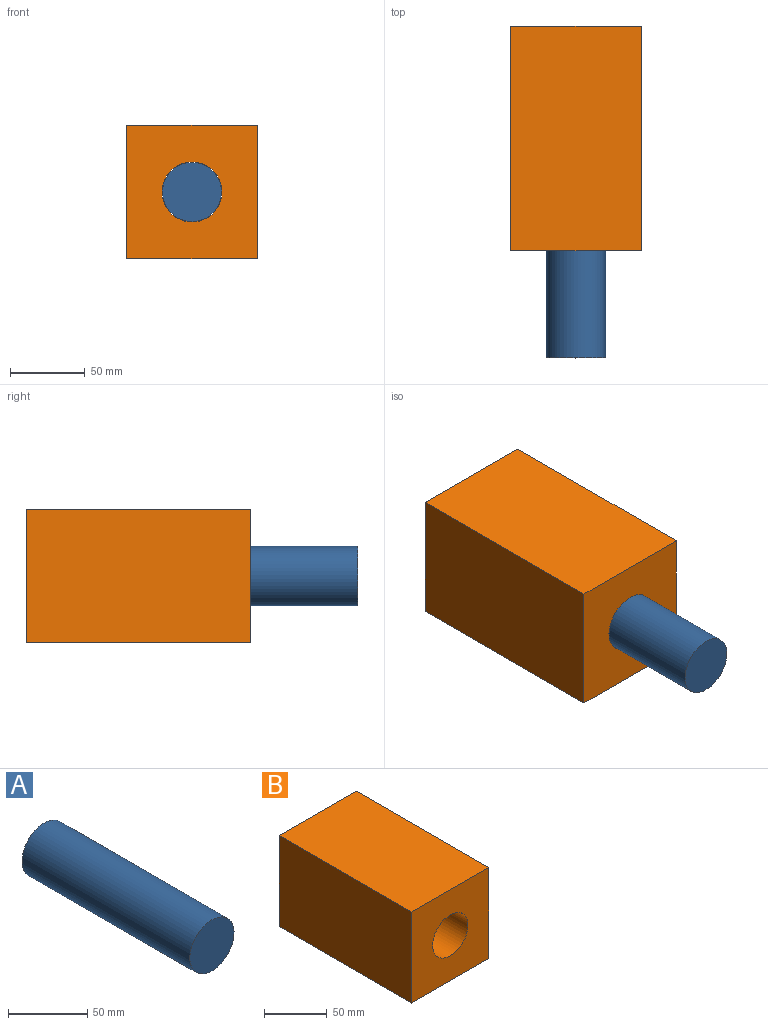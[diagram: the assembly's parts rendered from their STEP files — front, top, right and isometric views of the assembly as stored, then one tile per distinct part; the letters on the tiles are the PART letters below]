
ASSEMBLY  parts=2 mates=1
PART A: 3 faces, bbox 39.5x150x39.5 mm
  f0: cylinder r=19.75mm len=150mm, axis (0,1,0), area 18613.9mm2, adj f1,f2
  f1: plane 39.5x39.5mm, normal (0,-1,0), area 1225.4mm2, adj f0
  f2: plane 39.5x39.5mm, normal (0,1,0), area 1225.4mm2, adj f0
PART B: 7 faces, bbox 87.2x150x89.1 mm
  f0: plane 150x87.21mm, normal (0,0,-1), area 13082.1mm2, adj f1,f4,f5,f6
  f1: plane 150x89.07mm, normal (1,0,0), area 13360.4mm2, adj f0,f2,f5,f6
  f2: plane 150x87.21mm, normal (0,0,1), area 13082.1mm2, adj f1,f4,f5,f6
  f3: cylinder r=20mm len=150mm, axis (0,1,0), area 18849.6mm2, adj f5,f6
  f4: plane 150x89.07mm, normal (-1,0,0), area 13360.4mm2, adj f0,f2,f5,f6
  f5: plane 89.07x87.21mm, normal (0,1,0), area 6511.4mm2, adj f0,f1,f2,f3,f4
  f6: plane 89.07x87.21mm, normal (0,-1,0), area 6511.4mm2, adj f0,f1,f2,f3,f4
PLACE A t=(94.1,-130.96,-59.98)mm
PLACE B t=(217.43,-59.38,-55.07)mm fixed
MATE slider B.f3 <-> A.f0  axis (0,1,0) through (-29.83,-209.38,88.28)mm
